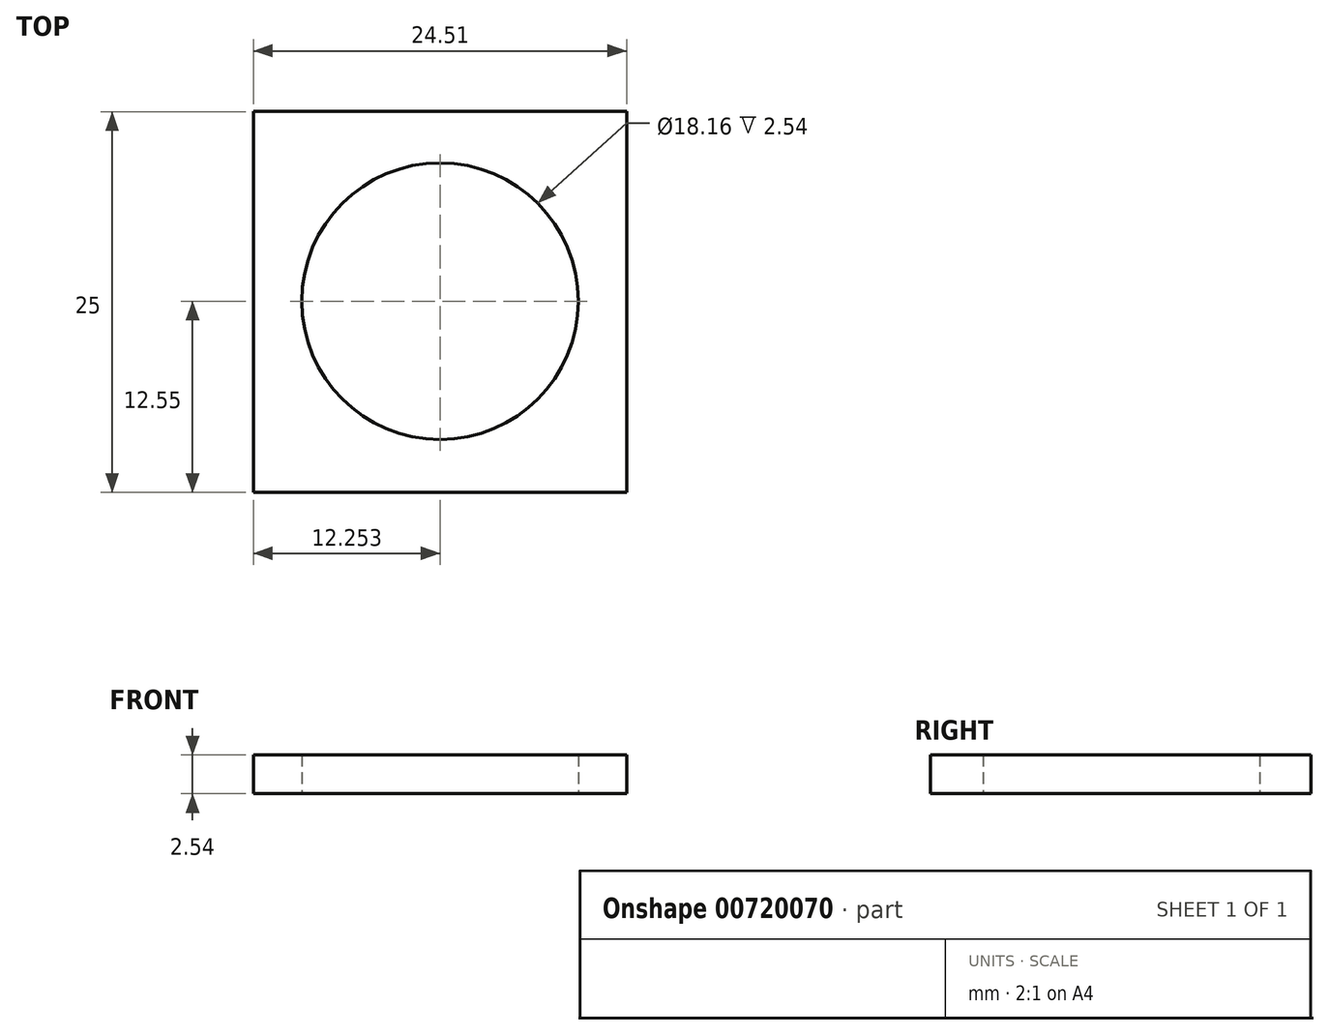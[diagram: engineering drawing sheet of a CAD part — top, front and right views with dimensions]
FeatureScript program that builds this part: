
annotation { "Feature Type Name" : "Feature", "Feature Type Description" : "" }
export const myFeature = defineFeature(function(context is Context, id is Id, definition is map)
    precondition{}
    {
        {
            var Q0;
            Q0=qCreatedBy(makeId("Top.planeOp"),FACE);
            var sketch = newSketch(context, id + "F0", { "sketchPlane" : qUnion([Q0])});
            skLineSegment(sketch, "E0", {"start": v(-28.5, 25) * mm, "end": v(-28.5, 0) * mm});
            skLineSegment(sketch, "E1", {"start": v(-28.5, 0) * mm, "end": v(-3.99, 0) * mm});
            skLineSegment(sketch, "E2", {"start": v(-3.99, 0) * mm, "end": v(-3.99, 25) * mm});
            skLineSegment(sketch, "E3", {"start": v(-3.99, 25) * mm, "end": v(-28.5, 25) * mm});
            skCircle(sketch, "E4", {"center": v(-16.25, 12.55) * mm, "radius": 9.08 * mm});
            skSolve(sketch);
        }
        {
            var Q0;
            Q0 = qSketchRegion(id + "F0", true);
            extrude(context, id + "F1", {"entities" : qUnion([Q0]), "depth" : 2.54 * mm, "offsetDistance" : 25.4 * mm});
        }
    });
